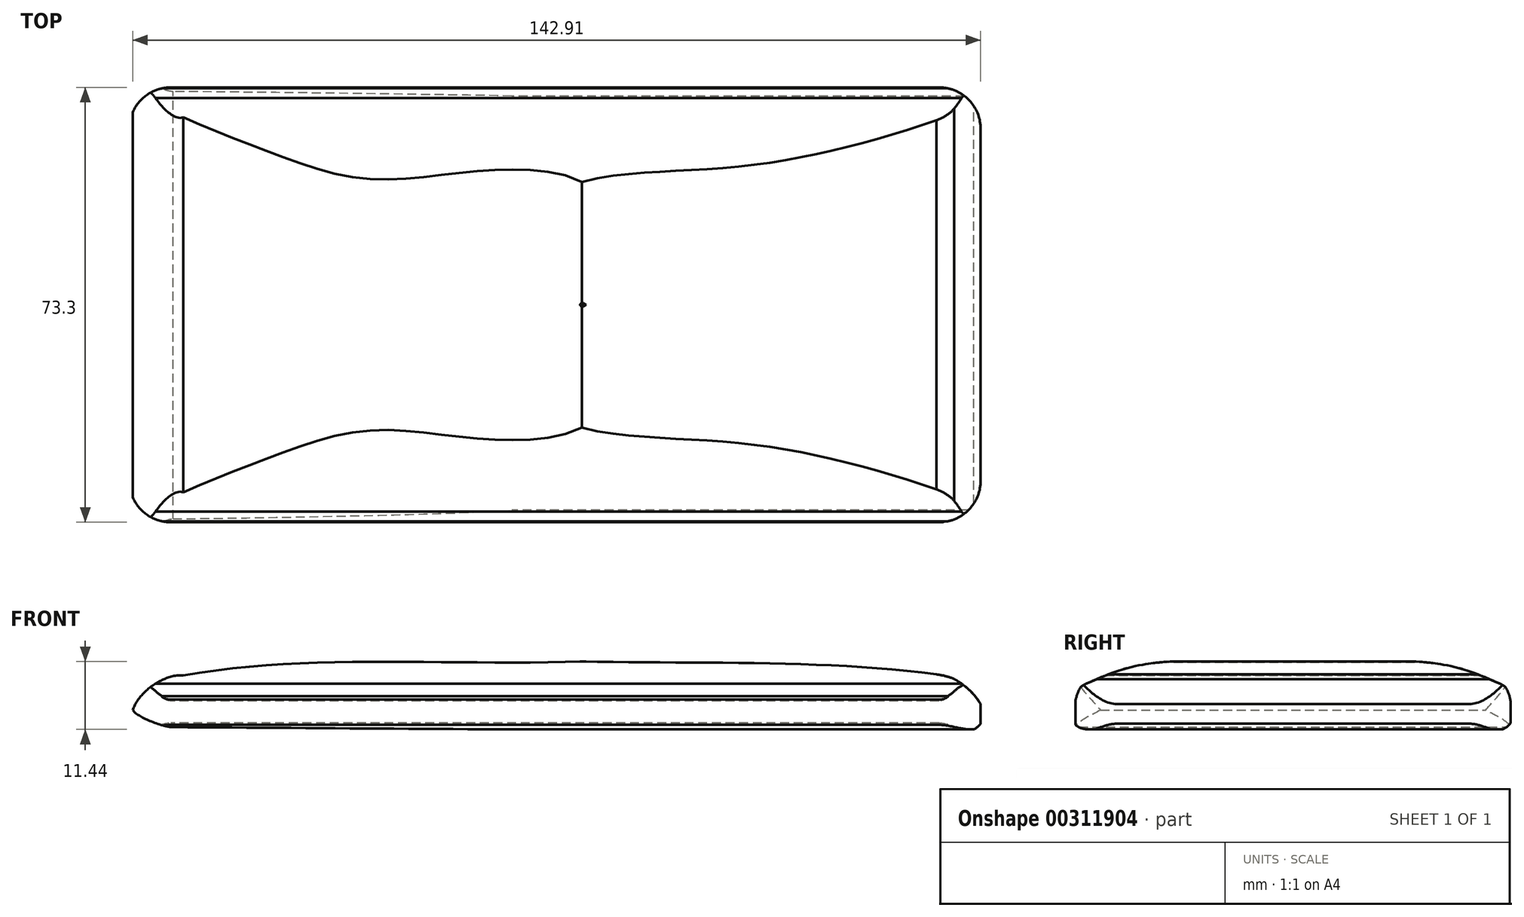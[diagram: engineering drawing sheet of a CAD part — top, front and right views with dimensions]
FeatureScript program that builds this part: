
annotation { "Feature Type Name" : "Feature", "Feature Type Description" : "" }
export const myFeature = defineFeature(function(context is Context, id is Id, definition is map)
    precondition{}
    {
        {
            var Q0;
            Q0=qCreatedBy(makeId("Front.planeOp"),FACE);
            var sketch = newSketch(context, id + "F0", { "sketchPlane" : qUnion([Q0])});
            skPoint(sketch, "E0.end.orphan", {"position": v(72.5, 0) * mm});
            skFitSpline(sketch, "E1", {"points": [v(72.5, -2.75) * mm, v(71.01, -5.37) * mm, v(68.19, -6.13) * mm], "startDerivative": vector(-0.5, -6.32) * mm, "endDerivative": vector(-6.6, -0.34) * mm});
            skFitSpline(sketch, "E2", {"points": [v(72.5, -2.75) * mm, v(67.28, 2.86) * mm], "startDerivative": vector(-2.33, 5.26) * mm, "endDerivative": vector(-8.17, 4.1) * mm});
            skFitSpline(sketch, "E3", {"points": [v(67.28, 2.86) * mm, v(64.31, 3.65) * mm], "startDerivative": vector(-1.75, 1.03) * mm, "endDerivative": vector(-2.63, 0.3) * mm});
            skFitSpline(sketch, "E4", {"points": [v(64.31, 3.65) * mm, v(4.57, 5.82) * mm], "startDerivative": vector(-53.35, 7.42) * mm, "endDerivative": vector(-61.84, 1.13) * mm});
            skFitSpline(sketch, "E5", {"points": [v(4.57, 5.82) * mm, v(-62.65, 3.45) * mm], "startDerivative": vector(-67.22, -2.3) * mm, "endDerivative": vector(-63.74, -11.57) * mm});
            skFitSpline(sketch, "E6", {"points": [v(-62.65, 3.45) * mm, v(-71.16, -2.35) * mm], "startDerivative": vector(-6.27, 1.28) * mm, "endDerivative": vector(-4.34, -11.92) * mm});
            skFitSpline(sketch, "E7", {"points": [v(-71.16, -2.35) * mm, v(-64.37, -5.24) * mm], "startDerivative": vector(2.67, -4.15) * mm, "endDerivative": vector(3.77, 0.2) * mm});
            skLineSegment(sketch, "E8", {"start": v(-64.37, -5.24) * mm, "end": v(68.19, -6.13) * mm});
            skSolve(sketch);
        }
        {
            var Q0;
            Q0=makeQuery(id+"F0.imprint","IMPRINT",FACE,{"disambiguationData":[TD([[makeQuery(id+"F0.imprint","IMPRINT",EDGE,{"derivedFrom":sQuery(id+"F0.wireOp",EDGE,"E0")}),1.0]])]});
            var Q1;
            Q1=makeQuery(id+"F0.imprint","IMPRINT",FACE,{"disambiguationData":[TD([[makeQuery(id+"F0.imprint","IMPRINT",EDGE,{"derivedFrom":sQuery(id+"F0.wireOp",EDGE,"E1")}),-1.0]])]});
            extrude(context, id + "F1", {"entities" : qUnion([Q0, Q1]), "endBound" : BoundingType.SYMMETRIC, "depth" : 80 * mm});
        }
        {
            var Q0;
            Q0=qCreatedBy(makeId("Right.planeOp"),FACE);
            var sketch = newSketch(context, id + "F2", { "sketchPlane" : qUnion([Q0])});
            skFitSpline(sketch, "E9", {"points": [v(34.88, 2.09) * mm, v(36.5, 0) * mm], "startDerivative": vector(3.02, -1.55) * mm, "endDerivative": vector(1.8, -4.71) * mm});
            skFitSpline(sketch, "E10", {"points": [v(0, 5.81) * mm, v(34.88, 2.09) * mm], "startDerivative": vector(73.4, 1.9) * mm, "endDerivative": vector(25.7, -11.17) * mm});
            skLineSegment(sketch, "E11", {"start": v(0, 5.81) * mm, "end": v(0, 0) * mm});
            skLineSegment(sketch, "E12", {"start": v(0, 0) * mm, "end": v(36.5, 0) * mm});
            skFitSpline(sketch, "E13.MirrorCS", {"points": [v(-34.88, 2.09) * mm, v(-36.5, 0) * mm], "startDerivative": vector(-3.02, -1.55) * mm, "endDerivative": vector(-1.8, -4.71) * mm});
            skLineSegment(sketch, "E14.MirrorCS", {"start": v(0, 0) * mm, "end": v(-36.5, 0) * mm});
            skFitSpline(sketch, "E15.MirrorCS", {"points": [v(0, 5.81) * mm, v(-34.88, 2.09) * mm], "startDerivative": vector(-73.4, 1.9) * mm, "endDerivative": vector(-25.7, -11.17) * mm});
            skCircle(sketch, "E16", {"center": v(0, 0) * mm, "radius": 42.9 * mm});
            skFitSpline(sketch, "E17", {"points": [v(36.5, 0) * mm, v(35.2, -5.62) * mm], "startDerivative": vector(0.65, -4.83) * mm, "endDerivative": vector(-8.6, -3.15) * mm});
            skFitSpline(sketch, "E18", {"points": [v(-34.63, -5.62) * mm, v(-36.5, 0) * mm], "startDerivative": vector(-14.1, 1.4) * mm, "endDerivative": vector(-0.57, 1) * mm});
            skLineSegment(sketch, "E19", {"start": v(35.2, -5.62) * mm, "end": v(-34.63, -5.62) * mm});
            skSolve(sketch);
        }
        {
            var Q0;
            Q0=makeQuery(id+"F2.imprint","IMPRINT",FACE,{"disambiguationData":[TD([[makeQuery(id+"F2.imprint","IMPRINT",EDGE,{"derivedFrom":sQuery(id+"F2.wireOp",EDGE,"E9")}),1.0]])]});
            extrude(context, id + "F3", {"entities" : qUnion([Q0]), "operationType" : NewBodyOperationType.REMOVE, "endBound" : BoundingType.SYMMETRIC, "depth" : 154.6 * mm});
        }
        {
            var Q0;
            Q0=makeQuery(id+"F3.boolean.opBoolean","COPY",FACE,{"derivedFrom":makeQuery(id+"F3.opExtrude","SWEPT_FACE",FACE,{"disambiguationData":[OSD([sQuery(id+"F2.wireOp",EDGE,"E19")])]})});
            var sketch = newSketch(context, id + "F4", { "sketchPlane" : qUnion([Q0])});
            skLineSegment(sketch, "E20.bottom", {"start": v(64.75, 36.65) * mm, "end": v(-64.75, 36.65) * mm});
            skLineSegment(sketch, "E20.top", {"start": v(64.75, -36.65) * mm, "end": v(-64.75, -36.65) * mm});
            skLineSegment(sketch, "E20.left", {"start": v(71.75, 29.65) * mm, "end": v(71.75, -29.65) * mm});
            skLineSegment(sketch, "E20.right", {"start": v(-71.75, 29.65) * mm, "end": v(-71.75, -29.65) * mm});
            skPoint(sketch, "E21.visualSharp", {"position": v(71.75, -36.65) * mm});
            skArc(sketch, "E21.filletArc", {"start": v(64.75, -36.65) * mm, "mid": v(69.7, -34.6) * mm, "end": v(71.75, -29.65) * mm});
            skPoint(sketch, "E22.visualSharp", {"position": v(71.75, 36.65) * mm});
            skArc(sketch, "E22.filletArc", {"start": v(71.75, 29.65) * mm, "mid": v(69.7, 34.6) * mm, "end": v(64.75, 36.65) * mm});
            skPoint(sketch, "E23.visualSharp", {"position": v(-71.75, -36.65) * mm});
            skArc(sketch, "E23.filletArc", {"start": v(-71.75, -29.65) * mm, "mid": v(-69.7, -34.6) * mm, "end": v(-64.75, -36.65) * mm});
            skPoint(sketch, "E24.visualSharp", {"position": v(-71.75, 36.65) * mm});
            skArc(sketch, "E24.filletArc", {"start": v(-64.75, 36.65) * mm, "mid": v(-69.7, 34.6) * mm, "end": v(-71.75, 29.65) * mm});
            skArc(sketch, "E25.0", {"start": v(76.75, 29.65) * mm, "mid": v(73.24, 38.14) * mm, "end": v(64.75, 41.65) * mm});
            skLineSegment(sketch, "E25.1", {"start": v(76.75, 29.65) * mm, "end": v(76.75, -29.65) * mm});
            skLineSegment(sketch, "E25.2", {"start": v(64.75, 41.65) * mm, "end": v(-64.75, 41.65) * mm});
            skArc(sketch, "E25.3", {"start": v(64.75, -41.65) * mm, "mid": v(73.24, -38.14) * mm, "end": v(76.75, -29.65) * mm});
            skArc(sketch, "E25.4", {"start": v(-64.75, 41.65) * mm, "mid": v(-73.24, 38.14) * mm, "end": v(-76.75, 29.65) * mm});
            skLineSegment(sketch, "E25.5", {"start": v(-76.75, 29.65) * mm, "end": v(-76.75, -29.65) * mm});
            skArc(sketch, "E25.6", {"start": v(-76.75, -29.65) * mm, "mid": v(-73.24, -38.14) * mm, "end": v(-64.75, -41.65) * mm});
            skLineSegment(sketch, "E25.7", {"start": v(64.75, -41.65) * mm, "end": v(-64.75, -41.65) * mm});
            skSolve(sketch);
        }
        {
            var Q0;
            {var subQ1=sQuery(id+"F4.wireOp",EDGE,"E20.bottom");Q0=makeQuery(id+"F4.imprint","IMPRINT",FACE,{"disambiguationData":[TD([[makeQuery(id+"F4.imprint","IMPRINT",EDGE,{"derivedFrom":subQ1}),-1.0]])]});}
            var Q1;
            {var subQ0=sQuery(id+"F4.wireOp",EDGE,"E22.filletArc");var subQ1=sQuery(id+"F2.wireOp",EDGE,"E19");var subQ2=makeQuery(id+"F3.boolean.opBoolean","INTERSECT",EDGE,{"derivedFrom":[makeQuery(id+"F1.opExtrude","SWEPT_FACE",FACE,{"disambiguationData":[OSD([sQuery(id+"F0.wireOp",EDGE,"E1")])]}),makeQuery(id+"F3.opExtrude","SWEPT_FACE",FACE,{"disambiguationData":[OSD([subQ1])]})]});var subQ3=makeQuery(id+"F4.imprint","INTERSECT",VERTEX,{"derivedFrom":[subQ2,subQ0]});Q1=makeQuery(id+"F4.imprint","IMPRINT",FACE,{"disambiguationData":[TD([[makeQuery(id+"F4.imprint","IMPRINT",EDGE,{"disambiguationData":[TD([[subQ3,-1.0]])],"derivedFrom":subQ0}),-1.0]])]});}
            var Q2;
            {var subQ0=sQuery(id+"F4.wireOp",EDGE,"E21.filletArc");var subQ1=sQuery(id+"F2.wireOp",EDGE,"E19");var subQ2=makeQuery(id+"F3.boolean.opBoolean","COPY",EDGE,{"derivedFrom":makeQuery(id+"F3.opExtrude","SWEPT_EDGE",EDGE,{"disambiguationData":[OSD([sQuery(id+"F2.wireOp",EDGE,"E17"),subQ1])]})});var subQ3=makeQuery(id+"F4.imprint","INTERSECT",VERTEX,{"derivedFrom":[subQ2,subQ0]});Q2=makeQuery(id+"F4.imprint","IMPRINT",FACE,{"disambiguationData":[TD([[makeQuery(id+"F4.imprint","IMPRINT",EDGE,{"disambiguationData":[TD([[subQ3,-1.0]])],"derivedFrom":subQ0}),-1.0]])]});}
            extrude(context, id + "F5", {"entities" : qUnion([Q0, Q1, Q2]), "operationType" : NewBodyOperationType.REMOVE, "oppositeDirection" : true, "depth" : 15 * mm});
        }
    });
